# Revit family: PipeAccessories_Valve_Oventrop_Cocon-QTR_DN40-50
name_source: partatom
category: Pipe Accessories
revit_build: Autodesk Revit 2014 (Build: 20140709_2115(x64)
units: mm (PartAtom-declared; Revit-internal decimal feet)

## types (1)
- QTR
    BodyMaterial = <By Category>
    ConnectorDescription = “classic”,both ports female thread according to EN 10226.
    Description = Pressure independent control valve (PICV). Both ports female
    HandleMaterial = <By Category>
    Lookup Table Name = PipeAccessories_Valve_Oventrop_Cocon-QTR_DN40-50
    Manufacturer = Oventrop
    Max.Pressure = PN 16
    Model = Cocon Q
    ModifiedIssue_ANZRS = 20141127.54 $
    PlugHeight = 32 mm  [stored 0.104987 ft]
    PlugRadius = 6 mm  [stored 0.019685 ft]
    SpindleMaterial = <By Category>
    Type Comments = Flow Threaded Bronze, 2 Pressure Test points
    URL = http://oventrop.de

note: [stored X ft] marks values corroborated as IEEE doubles in the binary element streams (Revit-internal decimal feet)

## geometry (parser evidence)
native form markers: Sweep x1
no freeform markers — native parametric forms only
